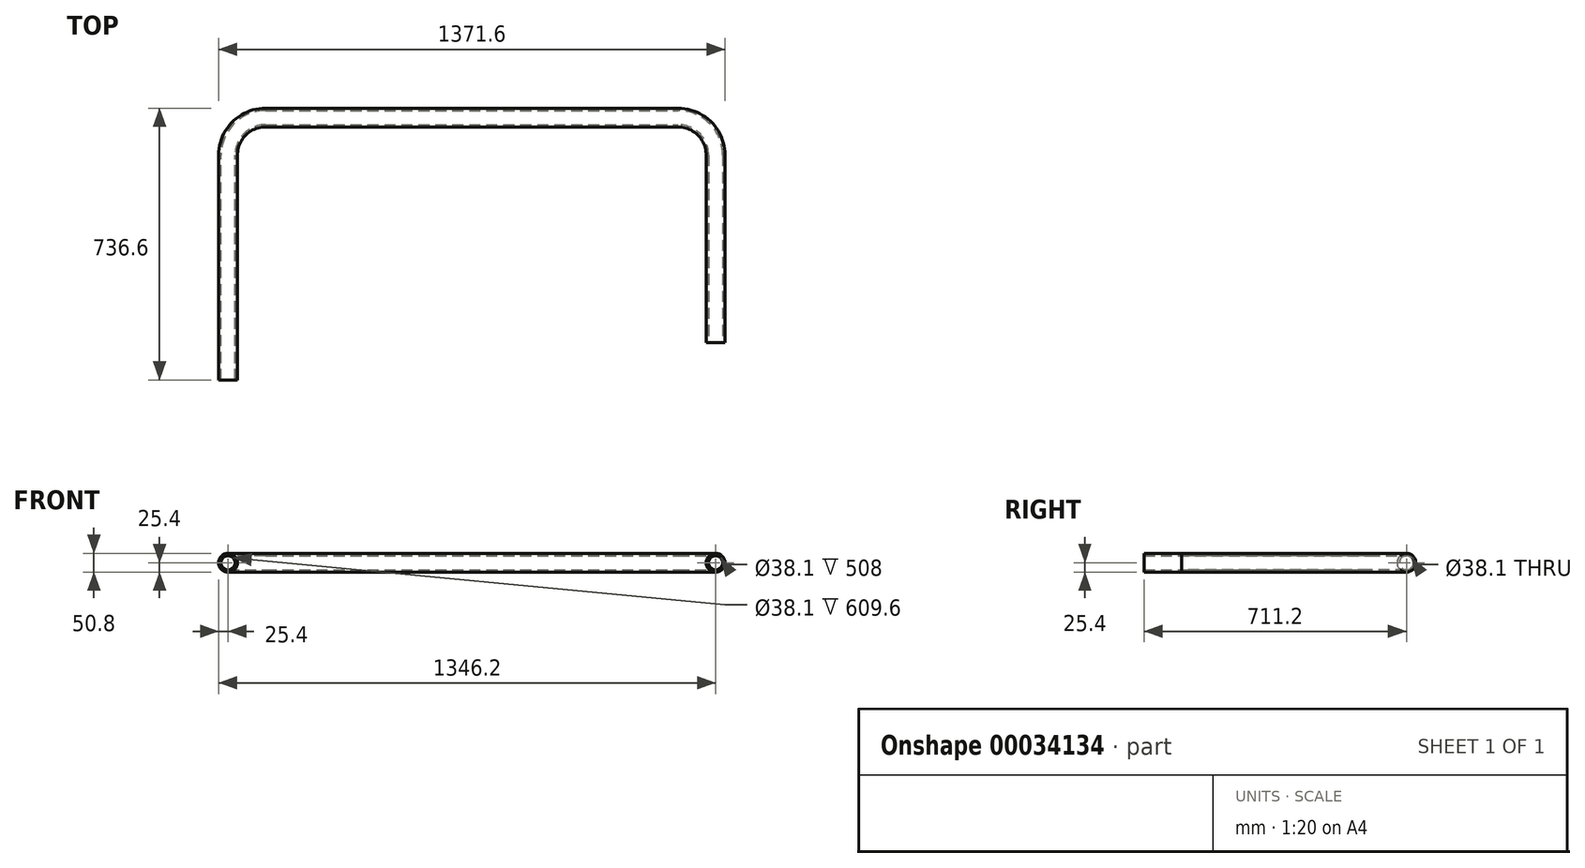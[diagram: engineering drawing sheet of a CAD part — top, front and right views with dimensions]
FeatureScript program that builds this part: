
annotation { "Feature Type Name" : "Feature", "Feature Type Description" : "" }
export const myFeature = defineFeature(function(context is Context, id is Id, definition is map)
    precondition{}
    {
        {
            var Q0;
            Q0=qCreatedBy(makeId("Front.planeOp"),FACE);
            var sketch = newSketch(context, id + "F0", { "sketchPlane" : qUnion([Q0])});
            skCircle(sketch, "E0", {"center": v(0, 0) * mm, "radius": 25.4 * mm});
            skCircle(sketch, "E1", {"center": v(0, 0) * mm, "radius": 19.05 * mm});
            skSolve(sketch);
        }
        {
            var Q0;
            Q0=qCreatedBy(makeId("Top.planeOp"),FACE);
            var sketch = newSketch(context, id + "F1", { "sketchPlane" : qUnion([Q0])});
            skLineSegment(sketch, "E2", {"start": v(0, 0) * mm, "end": v(0, 609.6) * mm});
            skLineSegment(sketch, "E3", {"start": v(101.6, 711.2) * mm, "end": v(1219.2, 711.2) * mm});
            skLineSegment(sketch, "E4", {"start": v(1320.8, 609.6) * mm, "end": v(1320.8, 101.6) * mm});
            skPoint(sketch, "E5.visualSharp", {"position": v(0, 711.2) * mm});
            skArc(sketch, "E5.filletArc", {"start": v(101.6, 711.2) * mm, "mid": v(29.76, 681.44) * mm, "end": v(0, 609.6) * mm});
            skPoint(sketch, "E6.visualSharp", {"position": v(1320.8, 711.2) * mm});
            skArc(sketch, "E6.filletArc", {"start": v(1320.8, 609.6) * mm, "mid": v(1291.04, 681.44) * mm, "end": v(1219.2, 711.2) * mm});
            skLineSegment(sketch, "E7", {"start": v(1219.2, 0) * mm, "end": v(1219.2, 0) * mm});
            skPoint(sketch, "E8.visualSharp", {"position": v(1320.8, 0) * mm});
            skArc(sketch, "E8.filletArc", {"start": v(1219.2, 0) * mm, "mid": v(1291.04, 29.76) * mm, "end": v(1320.8, 101.6) * mm});
            skSolve(sketch);
        }
        {
            var Q0;
            Q0=makeQuery(id+"F0.imprint","IMPRINT",FACE,{"disambiguationData":[TD([[makeQuery(id+"F0.imprint","IMPRINT",EDGE,{"derivedFrom":sQuery(id+"F0.wireOp",EDGE,"E0")}),1.0]])]});
            var Q1;
            Q1=sQuery(id+"F1.wireOp",EDGE,"E2");
            var Q2;
            Q2=sQuery(id+"F1.wireOp",EDGE,"E5.filletArc");
            var Q3;
            Q3=sQuery(id+"F1.wireOp",EDGE,"E3");
            var Q4;
            Q4=sQuery(id+"F1.wireOp",EDGE,"E6.filletArc");
            var Q5;
            Q5=sQuery(id+"F1.wireOp",EDGE,"E4");
            sweep(context, id + "F2", {"profiles" : qUnion([Q0]), "path" : qUnion([Q1, Q2, Q3, Q4, Q5])});
        }
    });
